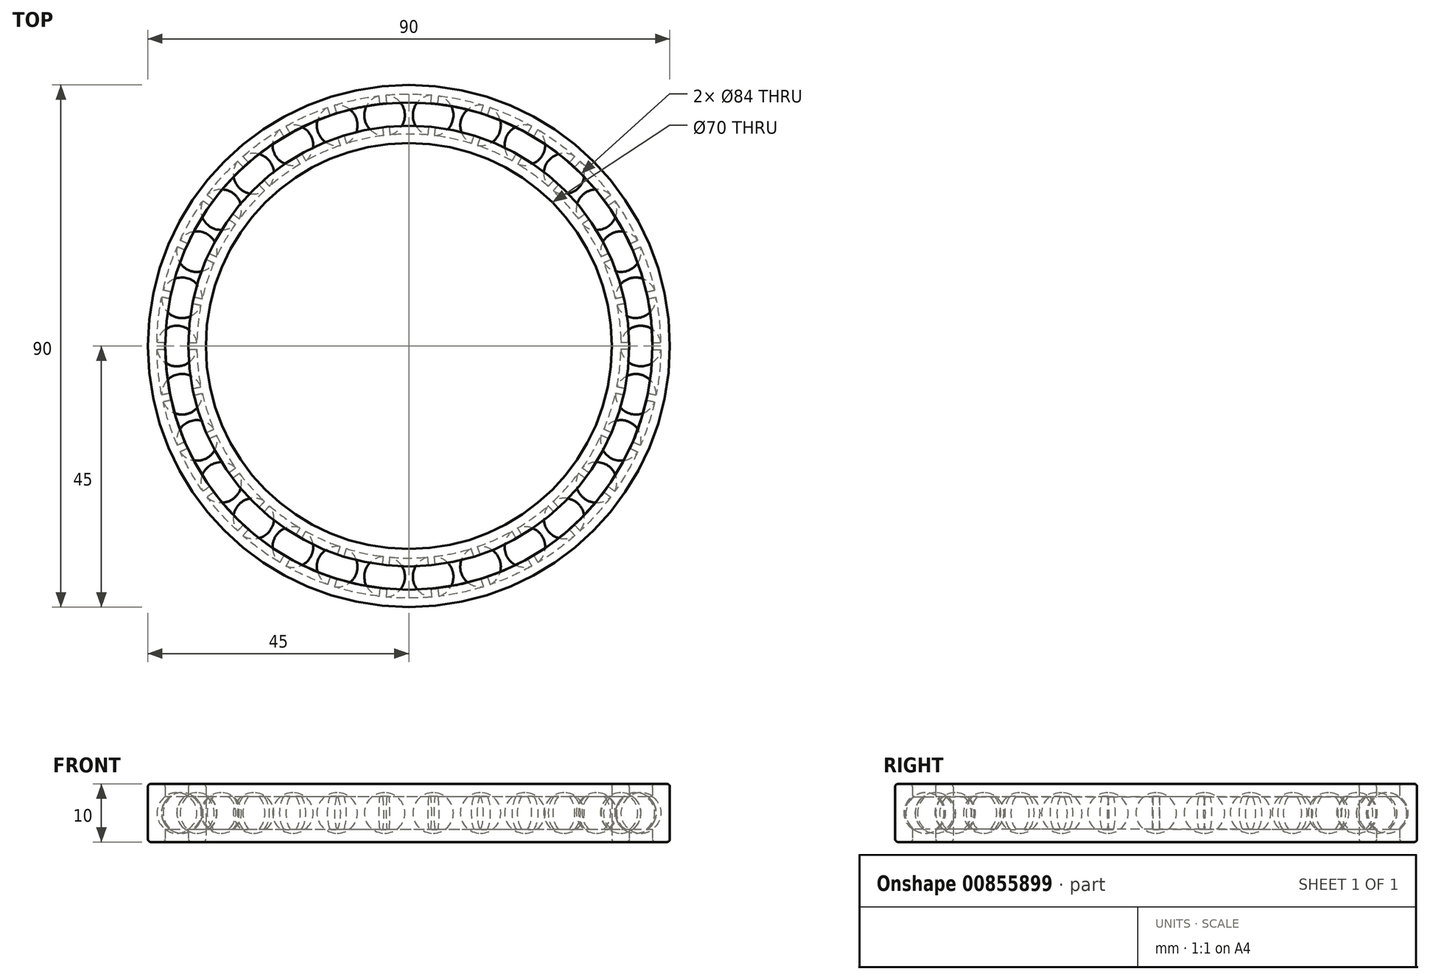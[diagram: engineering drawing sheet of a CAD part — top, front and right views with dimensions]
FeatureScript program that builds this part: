
annotation { "Feature Type Name" : "Feature", "Feature Type Description" : "" }
export const myFeature = defineFeature(function(context is Context, id is Id, definition is map)
    precondition{}
    {
        {
            var Q0;
            Q0=qCreatedBy(makeId("Front.planeOp"),FACE);
            var sketch = newSketch(context, id + "F0", { "sketchPlane" : qUnion([Q0])});
            skLineSegment(sketch, "E0.bottom", {"start": v(35, 5) * mm, "end": v(38, 5) * mm});
            skLineSegment(sketch, "E0.top", {"start": v(35, -5) * mm, "end": v(38, -5) * mm});
            skLineSegment(sketch, "E0.left", {"start": v(35, 5) * mm, "end": v(35, -5) * mm});
            skLineSegment(sketch, "E0.right", {"start": v(38, 5) * mm, "end": v(38, 2.81) * mm});
            skLineSegment(sketch, "E1.bottom", {"start": v(42, 5) * mm, "end": v(45, 5) * mm});
            skLineSegment(sketch, "E1.top", {"start": v(42, -5) * mm, "end": v(45, -5) * mm});
            skLineSegment(sketch, "E1.left", {"start": v(42, 5) * mm, "end": v(42, 2.81) * mm});
            skLineSegment(sketch, "E1.right", {"start": v(45, 5) * mm, "end": v(45, -5) * mm});
            skArc(sketch, "E2", {"start": v(38, 2.81) * mm, "mid": v(36.55, 0) * mm, "end": v(38, -2.81) * mm});
            skArc(sketch, "E3.trimOffspring", {"start": v(42, -2.81) * mm, "mid": v(43.45, 0) * mm, "end": v(42, 2.81) * mm});
            skLineSegment(sketch, "E4.trimOffspring", {"start": v(38, -2.81) * mm, "end": v(38, -5) * mm});
            skLineSegment(sketch, "E5.trimOffspring", {"start": v(42, -2.81) * mm, "end": v(42, -5) * mm});
            skSolve(sketch);
        }
        {
            var Q0;
            Q0=qCreatedBy(makeId("Right.planeOp"),FACE);
            var sketch = newSketch(context, id + "F1", { "sketchPlane" : qUnion([Q0])});
            skLineSegment(sketch, "E6", {"start": v(0, 0) * mm, "end": v(0, 39.58) * mm});
            skSolve(sketch);
        }
        {
            var Q0;
            Q0=qSketchRegion(id+"F0",true);
            var Q1;
            Q1=sQuery(id+"F1.wireOp",EDGE,"E6");
            revolve(context, id + "F2", {"surfaceOperationType" : NewSurfaceOperationType.NEW, "entities" : qUnion([Q0]), "axis" : qUnion([Q1]), "revolveType" : RevolveType.FULL});
        }
        {
            var Q0;
            Q0=qCreatedBy(makeId("Front.planeOp"),FACE);
            var sketch = newSketch(context, id + "F3", { "sketchPlane" : qUnion([Q0])});
            skArc(sketch, "E7", {"start": v(40, -3.5) * mm, "mid": v(43.5, 0) * mm, "end": v(40, 3.5) * mm});
            skLineSegment(sketch, "E8", {"start": v(40, 3.5) * mm, "end": v(40, -3.5) * mm});
            skSolve(sketch);
        }
        {
            var Q0;
            Q0=makeQuery(id+"F3.imprint","IMPRINT",FACE,{"disambiguationData":[TD([[makeQuery(id+"F3.imprint","IMPRINT",EDGE,{"derivedFrom":sQuery(id+"F3.wireOp",EDGE,"E7")}),1.0]])]});
            var Q1;
            Q1=sQuery(id+"F3.wireOp",EDGE,"E8");
            revolve(context, id + "F4", {"surfaceOperationType" : NewSurfaceOperationType.NEW, "entities" : qUnion([Q0]), "axis" : qUnion([Q1]), "revolveType" : RevolveType.FULL});
        }
        {
            var Q0;
            Q0=makeQuery(id+"F4.opRevolve","SWEPT_BODY",BODY,{"disambiguationData":[OSD([sQuery(id+"F3.wireOp",EDGE,"E7"),sQuery(id+"F3.wireOp",EDGE,"E8")])]});
            var Q1;
            Q1=makeQuery(id+"F2.opRevolve","SWEPT_EDGE",EDGE,{"disambiguationData":[OSD([sQuery(id+"F0.wireOp",EDGE,"E0.bottom"),sQuery(id+"F0.wireOp",EDGE,"E0.left")])]});
            circularPattern(context, id + "F5", {"operationType" : NewBodyOperationType.ADD, "entities" : qUnion([Q0]), "axis" : qUnion([Q1]), "angle" : 360 * degree, "instanceCount" : 30, "equalSpace" : true});
        }
        {
            var Q0;
            Q0=makeQuery(id+"F2.opRevolve","SWEPT_FACE",FACE,{"disambiguationData":[OSD([sQuery(id+"F0.wireOp",EDGE,"E0.bottom")])]});
            var Q1;
            Q1=makeQuery(id+"F2.opRevolve","SWEPT_FACE",FACE,{"disambiguationData":[OSD([sQuery(id+"F0.wireOp",EDGE,"E1.bottom")])]});
            var Q2;
            Q2=makeQuery(id+"F2.opRevolve","SWEPT_FACE",FACE,{"disambiguationData":[OSD([sQuery(id+"F0.wireOp",EDGE,"E0.top")])]});
            var Q3;
            Q3=makeQuery(id+"F2.opRevolve","SWEPT_FACE",FACE,{"disambiguationData":[OSD([sQuery(id+"F0.wireOp",EDGE,"E1.top")])]});
            fillet(context, id + "F6", {"entities" : qUnion([Q0, Q1, Q2, Q3]), "radius" : .5 * mm, "tangentPropagation" : true, "allowEdgeOverflow" : false});
        }
    });
